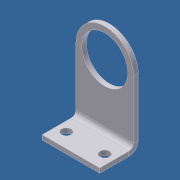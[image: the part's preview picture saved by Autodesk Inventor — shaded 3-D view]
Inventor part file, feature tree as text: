
AUTODESK INVENTOR PART (.ipt)
format: ipt  version: unknown  size: 212,992 bytes
history: native  units: in
note: dims shown in document units (in); Inventor stores cm internally (conversion verified against a paired STEP export)
features: sheet_metal_op x4, sketch x3, other x2, extrude x1
ambient origin geometry x8: Origin, YZ Plane, XZ Plane, XY Plane, X Axis, Y Axis, Z Axis, Center Point
bodies: Solid1 (feature_tree)
feature tree (10):
  sheet_metal_op  "Face1"
  sheet_metal_op  "Flange1"
  extrude  "Extrusion1"  Depth=2.5in
  sketch  "Sketch1"  dims[d0=1.5in d1=2.5in]
  other  "Plate1"
  sketch  "Sketch2"  dims[d2=0.0in]
  other  "Plate2"
  sheet_metal_op  "Bend1"
  sheet_metal_op  "Corner1"
  sketch  "Sketch3"  dims[d3=0.0in d4=1.2in d5=0.12in d6=0.12in d7=0.06in d8=0.24in d9=0.12in d10=1.0in d11=90.0deg d12=0.12in d13=0.48in d14=0.12in d15=0.12in d16=0.25in d17=1.0in d18=0.25in d19=1.0in d20=0.0in]
